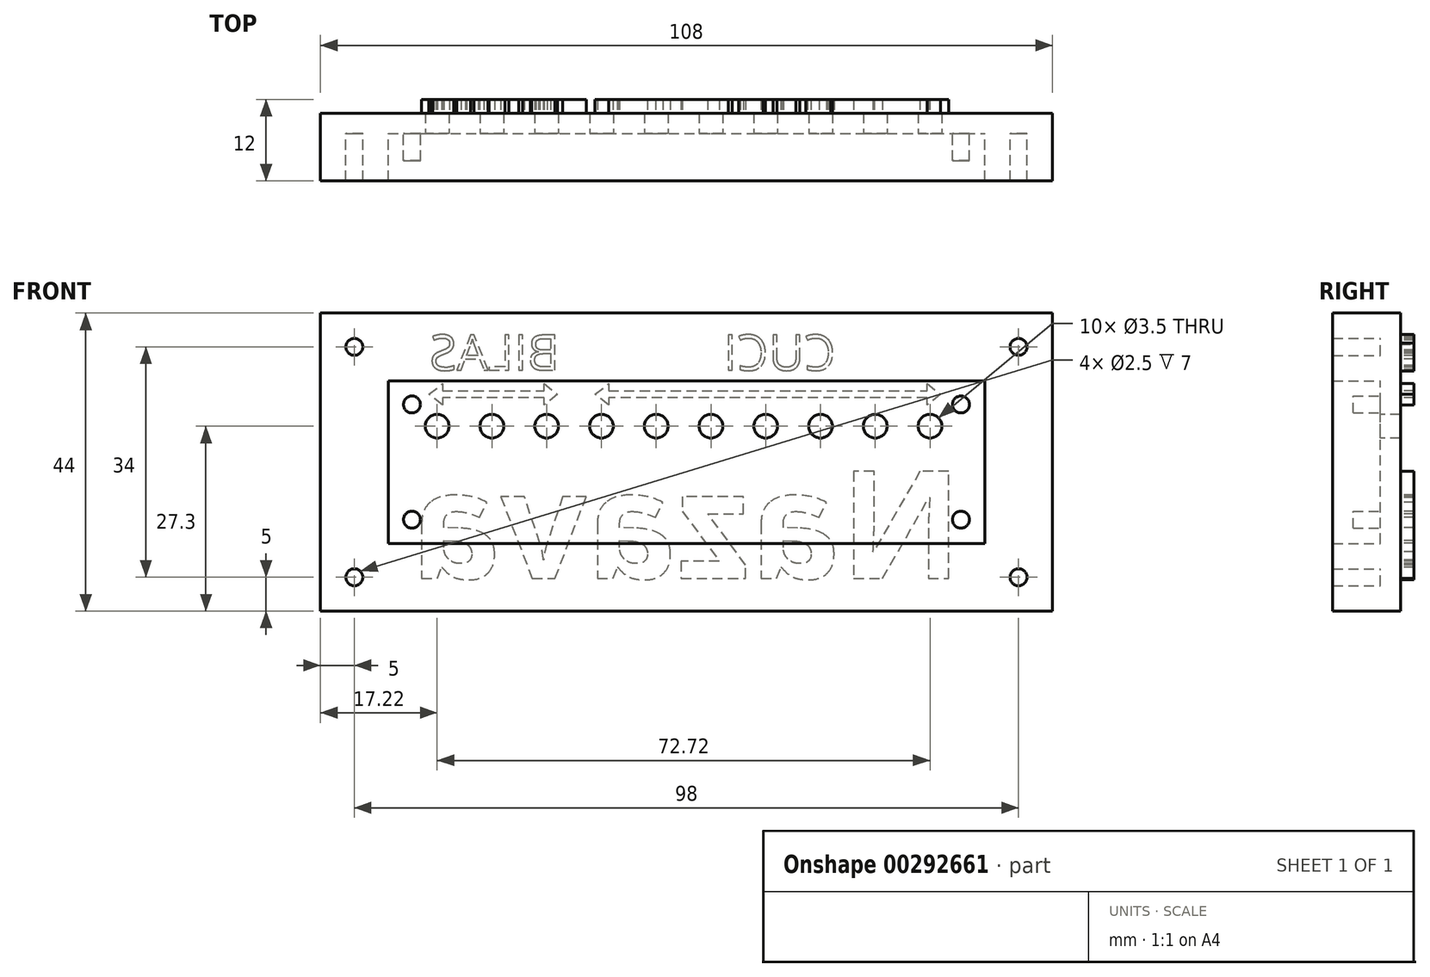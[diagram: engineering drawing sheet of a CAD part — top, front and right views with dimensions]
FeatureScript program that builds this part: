
annotation { "Feature Type Name" : "Feature", "Feature Type Description" : "" }
export const myFeature = defineFeature(function(context is Context, id is Id, definition is map)
    precondition{}
    {
        {
            var Q0;
            Q0=qCreatedBy(makeId("Front.planeOp"),FACE);
            var sketch = newSketch(context, id + "F0", { "sketchPlane" : qUnion([Q0])});
            skLineSegment(sketch, "E0.bottom", {"start": v(0, 0) * mm, "end": v(88, 0) * mm});
            skLineSegment(sketch, "E0.top", {"start": v(0, 24) * mm, "end": v(88, 24) * mm});
            skLineSegment(sketch, "E0.left", {"start": v(0, 0) * mm, "end": v(0, 24) * mm});
            skLineSegment(sketch, "E0.right", {"start": v(88, 0) * mm, "end": v(88, 24) * mm});
            skCircle(sketch, "E1", {"center": v(3.5, 20.5) * mm, "radius": 1.25 * mm});
            skCircle(sketch, "E2.0.1.0", {"center": v(3.5, 3.5) * mm, "radius": 1.25 * mm});
            skCircle(sketch, "E2.1.0.0", {"center": v(84.5, 20.5) * mm, "radius": 1.25 * mm});
            skCircle(sketch, "E2.1.1.0", {"center": v(84.5, 3.5) * mm, "radius": 1.25 * mm});
            skLineSegment(sketch, "E2.direction1", {"start": v(3.5, 20.5) * mm, "end": v(84.5, 20.5) * mm, "construction": true});
            skLineSegment(sketch, "E2.direction2", {"start": v(3.5, 20.5) * mm, "end": v(3.5, 3.5) * mm, "construction": true});
            skLineSegment(sketch, "E3.0", {"start": v(-10, 34) * mm, "end": v(98, 34) * mm});
            skLineSegment(sketch, "E3.1", {"start": v(-10, -10) * mm, "end": v(-10, 34) * mm});
            skLineSegment(sketch, "E3.2", {"start": v(-10, -10) * mm, "end": v(98, -10) * mm});
            skLineSegment(sketch, "E3.3", {"start": v(98, -10) * mm, "end": v(98, 34) * mm});
            skCircle(sketch, "E4", {"center": v(7.22, 17.3) * mm, "radius": 1.75 * mm});
            skCircle(sketch, "E5.1.0.0", {"center": v(15.3, 17.3) * mm, "radius": 1.75 * mm});
            skCircle(sketch, "E5.2.0.0", {"center": v(23.38, 17.3) * mm, "radius": 1.75 * mm});
            skCircle(sketch, "E5.3.0.0", {"center": v(31.46, 17.3) * mm, "radius": 1.75 * mm});
            skCircle(sketch, "E5.4.0.0", {"center": v(39.54, 17.3) * mm, "radius": 1.75 * mm});
            skCircle(sketch, "E5.5.0.0", {"center": v(47.62, 17.3) * mm, "radius": 1.75 * mm});
            skCircle(sketch, "E5.6.0.0", {"center": v(55.7, 17.3) * mm, "radius": 1.75 * mm});
            skCircle(sketch, "E5.7.0.0", {"center": v(63.78, 17.3) * mm, "radius": 1.75 * mm});
            skCircle(sketch, "E5.8.0.0", {"center": v(71.86, 17.3) * mm, "radius": 1.75 * mm});
            skCircle(sketch, "E5.9.0.0", {"center": v(79.94, 17.3) * mm, "radius": 1.75 * mm});
            skLineSegment(sketch, "E5.direction1", {"start": v(7.22, 17.3) * mm, "end": v(15.3, 17.3) * mm, "construction": true});
            skCircle(sketch, "E6", {"center": v(-5, 29) * mm, "radius": 1.25 * mm});
            skCircle(sketch, "E7.0.1.0", {"center": v(-5, -5) * mm, "radius": 1.25 * mm});
            skCircle(sketch, "E7.1.0.0", {"center": v(93, 29) * mm, "radius": 1.25 * mm});
            skCircle(sketch, "E7.1.1.0", {"center": v(93, -5) * mm, "radius": 1.25 * mm});
            skLineSegment(sketch, "E7.direction1", {"start": v(-5, 29) * mm, "end": v(93, 29) * mm, "construction": true});
            skLineSegment(sketch, "E7.direction2", {"start": v(-5, 29) * mm, "end": v(-5, -5) * mm, "construction": true});
            skSolve(sketch);
        }
        {
            var Q0;
            Q0=makeQuery(id+"F0.imprint","IMPRINT",FACE,{"disambiguationData":[TD([[makeQuery(id+"F0.imprint","IMPRINT",EDGE,{"derivedFrom":sQuery(id+"F0.wireOp",EDGE,"E0.bottom")}),-1.0]])]});
            var Q1;
            Q1=makeQuery(id+"F0.imprint","IMPRINT",FACE,{"disambiguationData":[TD([[makeQuery(id+"F0.imprint","IMPRINT",EDGE,{"derivedFrom":sQuery(id+"F0.wireOp",EDGE,"E0.bottom")}),1.0]])]});
            var Q2;
            Q2=makeQuery(id+"F0.imprint","IMPRINT",FACE,{"disambiguationData":[TD([[makeQuery(id+"F0.imprint","IMPRINT",EDGE,{"derivedFrom":sQuery(id+"F0.wireOp",EDGE,"E5.6.0.0")}),1.0]])]});
            var Q3;
            Q3=makeQuery(id+"F0.imprint","IMPRINT",FACE,{"disambiguationData":[TD([[makeQuery(id+"F0.imprint","IMPRINT",EDGE,{"derivedFrom":sQuery(id+"F0.wireOp",EDGE,"E2.1.1.0")}),1.0]])]});
            var Q4;
            Q4=makeQuery(id+"F0.imprint","IMPRINT",FACE,{"disambiguationData":[TD([[makeQuery(id+"F0.imprint","IMPRINT",EDGE,{"derivedFrom":sQuery(id+"F0.wireOp",EDGE,"E5.8.0.0")}),1.0]])]});
            var Q5;
            Q5=makeQuery(id+"F0.imprint","IMPRINT",FACE,{"disambiguationData":[TD([[makeQuery(id+"F0.imprint","IMPRINT",EDGE,{"derivedFrom":sQuery(id+"F0.wireOp",EDGE,"E5.7.0.0")}),1.0]])]});
            var Q6;
            Q6=makeQuery(id+"F0.imprint","IMPRINT",FACE,{"disambiguationData":[TD([[makeQuery(id+"F0.imprint","IMPRINT",EDGE,{"derivedFrom":sQuery(id+"F0.wireOp",EDGE,"E5.4.0.0")}),1.0]])]});
            var Q7;
            Q7=makeQuery(id+"F0.imprint","IMPRINT",FACE,{"disambiguationData":[TD([[makeQuery(id+"F0.imprint","IMPRINT",EDGE,{"derivedFrom":sQuery(id+"F0.wireOp",EDGE,"E5.5.0.0")}),1.0]])]});
            var Q8;
            Q8=makeQuery(id+"F0.imprint","IMPRINT",FACE,{"disambiguationData":[TD([[makeQuery(id+"F0.imprint","IMPRINT",EDGE,{"derivedFrom":sQuery(id+"F0.wireOp",EDGE,"E5.2.0.0")}),1.0]])]});
            var Q9;
            Q9=makeQuery(id+"F0.imprint","IMPRINT",FACE,{"disambiguationData":[TD([[makeQuery(id+"F0.imprint","IMPRINT",EDGE,{"derivedFrom":sQuery(id+"F0.wireOp",EDGE,"E5.9.0.0")}),1.0]])]});
            var Q10;
            Q10=makeQuery(id+"F0.imprint","IMPRINT",FACE,{"disambiguationData":[TD([[makeQuery(id+"F0.imprint","IMPRINT",EDGE,{"derivedFrom":sQuery(id+"F0.wireOp",EDGE,"E5.3.0.0")}),1.0]])]});
            var Q11;
            Q11=makeQuery(id+"F0.imprint","IMPRINT",FACE,{"disambiguationData":[TD([[makeQuery(id+"F0.imprint","IMPRINT",EDGE,{"derivedFrom":sQuery(id+"F0.wireOp",EDGE,"E2.0.1.0")}),1.0]])]});
            var Q12;
            Q12=makeQuery(id+"F0.imprint","IMPRINT",FACE,{"disambiguationData":[TD([[makeQuery(id+"F0.imprint","IMPRINT",EDGE,{"derivedFrom":sQuery(id+"F0.wireOp",EDGE,"E2.1.0.0")}),1.0]])]});
            var Q13;
            Q13=makeQuery(id+"F0.imprint","IMPRINT",FACE,{"disambiguationData":[TD([[makeQuery(id+"F0.imprint","IMPRINT",EDGE,{"derivedFrom":sQuery(id+"F0.wireOp",EDGE,"E5.1.0.0")}),1.0]])]});
            var Q14;
            Q14=makeQuery(id+"F0.imprint","IMPRINT",FACE,{"disambiguationData":[TD([[makeQuery(id+"F0.imprint","IMPRINT",EDGE,{"derivedFrom":sQuery(id+"F0.wireOp",EDGE,"E4")}),1.0]])]});
            var Q15;
            Q15=makeQuery(id+"F0.imprint","IMPRINT",FACE,{"disambiguationData":[TD([[makeQuery(id+"F0.imprint","IMPRINT",EDGE,{"derivedFrom":sQuery(id+"F0.wireOp",EDGE,"E1")}),1.0]])]});
            var Q16;
            Q16=makeQuery(id+"F0.imprint","IMPRINT",FACE,{"disambiguationData":[TD([[makeQuery(id+"F0.imprint","IMPRINT",EDGE,{"derivedFrom":sQuery(id+"F0.wireOp",EDGE,"E7.1.0.0")}),1.0]])]});
            var Q17;
            Q17=makeQuery(id+"F0.imprint","IMPRINT",FACE,{"disambiguationData":[TD([[makeQuery(id+"F0.imprint","IMPRINT",EDGE,{"derivedFrom":sQuery(id+"F0.wireOp",EDGE,"E6")}),1.0]])]});
            var Q18;
            Q18=makeQuery(id+"F0.imprint","IMPRINT",FACE,{"disambiguationData":[TD([[makeQuery(id+"F0.imprint","IMPRINT",EDGE,{"derivedFrom":sQuery(id+"F0.wireOp",EDGE,"E7.0.1.0")}),1.0]])]});
            var Q19;
            Q19=makeQuery(id+"F0.imprint","IMPRINT",FACE,{"disambiguationData":[TD([[makeQuery(id+"F0.imprint","IMPRINT",EDGE,{"derivedFrom":sQuery(id+"F0.wireOp",EDGE,"E7.1.1.0")}),1.0]])]});
            extrude(context, id + "F1", {"entities" : qUnion([Q0, Q1, Q2, Q3, Q4, Q5, Q6, Q7, Q8, Q9, Q10, Q11, Q12, Q13, Q14, Q15, Q16, Q17, Q18, Q19]), "oppositeDirection" : true, "depth" : 3 * mm, "offsetDistance" : 25 * mm});
        }
        {
            var Q0;
            Q0=makeQuery(id+"F0.imprint","IMPRINT",FACE,{"disambiguationData":[TD([[makeQuery(id+"F0.imprint","IMPRINT",EDGE,{"derivedFrom":sQuery(id+"F0.wireOp",EDGE,"E5.9.0.0")}),1.0]])]});
            var Q1;
            Q1=makeQuery(id+"F0.imprint","IMPRINT",FACE,{"disambiguationData":[TD([[makeQuery(id+"F0.imprint","IMPRINT",EDGE,{"derivedFrom":sQuery(id+"F0.wireOp",EDGE,"E5.8.0.0")}),1.0]])]});
            var Q2;
            Q2=makeQuery(id+"F0.imprint","IMPRINT",FACE,{"disambiguationData":[TD([[makeQuery(id+"F0.imprint","IMPRINT",EDGE,{"derivedFrom":sQuery(id+"F0.wireOp",EDGE,"E5.7.0.0")}),1.0]])]});
            var Q3;
            Q3=makeQuery(id+"F0.imprint","IMPRINT",FACE,{"disambiguationData":[TD([[makeQuery(id+"F0.imprint","IMPRINT",EDGE,{"derivedFrom":sQuery(id+"F0.wireOp",EDGE,"E5.6.0.0")}),1.0]])]});
            var Q4;
            Q4=makeQuery(id+"F0.imprint","IMPRINT",FACE,{"disambiguationData":[TD([[makeQuery(id+"F0.imprint","IMPRINT",EDGE,{"derivedFrom":sQuery(id+"F0.wireOp",EDGE,"E5.5.0.0")}),1.0]])]});
            var Q5;
            Q5=makeQuery(id+"F0.imprint","IMPRINT",FACE,{"disambiguationData":[TD([[makeQuery(id+"F0.imprint","IMPRINT",EDGE,{"derivedFrom":sQuery(id+"F0.wireOp",EDGE,"E5.4.0.0")}),1.0]])]});
            var Q6;
            Q6=makeQuery(id+"F0.imprint","IMPRINT",FACE,{"disambiguationData":[TD([[makeQuery(id+"F0.imprint","IMPRINT",EDGE,{"derivedFrom":sQuery(id+"F0.wireOp",EDGE,"E5.3.0.0")}),1.0]])]});
            var Q7;
            Q7=makeQuery(id+"F0.imprint","IMPRINT",FACE,{"disambiguationData":[TD([[makeQuery(id+"F0.imprint","IMPRINT",EDGE,{"derivedFrom":sQuery(id+"F0.wireOp",EDGE,"E5.2.0.0")}),1.0]])]});
            var Q8;
            Q8=makeQuery(id+"F0.imprint","IMPRINT",FACE,{"disambiguationData":[TD([[makeQuery(id+"F0.imprint","IMPRINT",EDGE,{"derivedFrom":sQuery(id+"F0.wireOp",EDGE,"E5.1.0.0")}),1.0]])]});
            var Q9;
            Q9=makeQuery(id+"F0.imprint","IMPRINT",FACE,{"disambiguationData":[TD([[makeQuery(id+"F0.imprint","IMPRINT",EDGE,{"derivedFrom":sQuery(id+"F0.wireOp",EDGE,"E4")}),1.0]])]});
            extrude(context, id + "F2", {"entities" : qUnion([Q0, Q1, Q2, Q3, Q4, Q5, Q6, Q7, Q8, Q9]), "operationType" : NewBodyOperationType.REMOVE, "endBound" : BoundingType.THROUGH_ALL, "oppositeDirection" : true, "depth" : 25 * mm, "offsetDistance" : 25 * mm});
        }
        {
            var Q0;
            Q0=makeQuery(id+"F0.imprint","IMPRINT",FACE,{"disambiguationData":[TD([[makeQuery(id+"F0.imprint","IMPRINT",EDGE,{"derivedFrom":sQuery(id+"F0.wireOp",EDGE,"E1")}),1.0]])]});
            var Q1;
            Q1=makeQuery(id+"F0.imprint","IMPRINT",FACE,{"disambiguationData":[TD([[makeQuery(id+"F0.imprint","IMPRINT",EDGE,{"derivedFrom":sQuery(id+"F0.wireOp",EDGE,"E2.1.0.0")}),1.0]])]});
            var Q2;
            Q2=makeQuery(id+"F0.imprint","IMPRINT",FACE,{"disambiguationData":[TD([[makeQuery(id+"F0.imprint","IMPRINT",EDGE,{"derivedFrom":sQuery(id+"F0.wireOp",EDGE,"E2.1.1.0")}),1.0]])]});
            var Q3;
            Q3=makeQuery(id+"F0.imprint","IMPRINT",FACE,{"disambiguationData":[TD([[makeQuery(id+"F0.imprint","IMPRINT",EDGE,{"derivedFrom":sQuery(id+"F0.wireOp",EDGE,"E2.0.1.0")}),1.0]])]});
            extrude(context, id + "F3", {"entities" : qUnion([Q0, Q1, Q2, Q3]), "operationType" : NewBodyOperationType.ADD, "depth" : 4 * mm, "offsetDistance" : 25 * mm});
        }
        {
            var Q0;
            Q0=makeQuery(id+"F0.imprint","IMPRINT",FACE,{"disambiguationData":[TD([[makeQuery(id+"F0.imprint","IMPRINT",EDGE,{"derivedFrom":sQuery(id+"F0.wireOp",EDGE,"E0.bottom")}),-1.0]])]});
            extrude(context, id + "F4", {"entities" : qUnion([Q0]), "operationType" : NewBodyOperationType.ADD, "depth" : 7 * mm, "offsetDistance" : 25 * mm});
        }
        {
            var Q0;
            Q0=makeQuery(id+"F1.opExtrude","CAP_FACE",FACE,{"disambiguationData":[OSD([sQuery(id+"F0.wireOp",EDGE,"E3.0"),sQuery(id+"F0.wireOp",EDGE,"E3.1"),sQuery(id+"F0.wireOp",EDGE,"E3.2"),sQuery(id+"F0.wireOp",EDGE,"E3.3")])],"isStart":false});
            var sketch = newSketch(context, id + "F5", { "sketchPlane" : qUnion([Q0])});
            skText(sketch, "E8", { "text": "Nazava", "fontName": "OpenSans-Bold.ttf"});
            const initialGuessF5  = {"E8": [-0.08468, -0.00517, 1, 0, 0.01592]};
            skSetInitialGuess(sketch, initialGuessF5);
            skSolve(sketch);
        }
        {
            var Q0;
            {var subQ0=sQuery(id+"F0.wireOp",EDGE,"E3.3");var subQ1=sQuery(id+"F0.wireOp",EDGE,"E3.0");var subQ2=sQuery(id+"F0.wireOp",EDGE,"E3.2");var subQ3=sQuery(id+"F0.wireOp",EDGE,"E3.1");Q0=makeQuery(id+"F8.boolean.opBoolean","SPLIT",FACE,{"disambiguationData":[TD([makeQuery(id+"F1.opExtrude","SWEPT_FACE",FACE,{"disambiguationData":[OSD([subQ1])]})])],"derivedFrom":makeQuery(id+"F1.opExtrude","CAP_FACE",FACE,{"disambiguationData":[OSD([subQ1,subQ3,subQ2,subQ0])],"isStart":false})});}
            var sketch = newSketch(context, id + "F6", { "sketchPlane" : qUnion([Q0])});
            skLineSegment(sketch, "E9", {"start": v(-30.5, 22) * mm, "end": v(-32.5, 23.57) * mm});
            skLineSegment(sketch, "E10", {"start": v(-32.5, 23.57) * mm, "end": v(-32.5, 22.5) * mm});
            skLineSegment(sketch, "E11", {"start": v(-32.5, 22.5) * mm, "end": v(-79.5, 22.5) * mm});
            skLineSegment(sketch, "E12", {"start": v(-79.5, 22.5) * mm, "end": v(-79.5, 23.57) * mm});
            skLineSegment(sketch, "E13", {"start": v(-79.5, 23.57) * mm, "end": v(-81.5, 22) * mm});
            skLineSegment(sketch, "E14", {"start": v(-81.5, 22) * mm, "end": v(-79.5, 20.43) * mm});
            skLineSegment(sketch, "E15", {"start": v(-79.5, 20.43) * mm, "end": v(-79.5, 21.5) * mm});
            skLineSegment(sketch, "E16", {"start": v(-79.5, 21.5) * mm, "end": v(-32.5, 21.5) * mm});
            skLineSegment(sketch, "E17", {"start": v(-32.5, 21.5) * mm, "end": v(-32.5, 20.43) * mm});
            skLineSegment(sketch, "E18", {"start": v(-32.5, 20.43) * mm, "end": v(-30.5, 22) * mm});
            skLineSegment(sketch, "E19", {"start": v(-5.99, 22) * mm, "end": v(-7.99, 23.57) * mm});
            skLineSegment(sketch, "E20", {"start": v(-7.99, 23.57) * mm, "end": v(-7.99, 22.5) * mm});
            skLineSegment(sketch, "E21", {"start": v(-7.99, 22.5) * mm, "end": v(-22.99, 22.5) * mm});
            skLineSegment(sketch, "E22", {"start": v(-22.99, 22.5) * mm, "end": v(-22.99, 23.57) * mm});
            skLineSegment(sketch, "E23", {"start": v(-22.99, 23.57) * mm, "end": v(-24.99, 22) * mm});
            skLineSegment(sketch, "E24", {"start": v(-24.99, 22) * mm, "end": v(-22.99, 20.43) * mm});
            skLineSegment(sketch, "E25", {"start": v(-22.99, 20.43) * mm, "end": v(-22.99, 21.5) * mm});
            skLineSegment(sketch, "E26", {"start": v(-22.99, 21.5) * mm, "end": v(-7.99, 21.5) * mm});
            skLineSegment(sketch, "E27", {"start": v(-7.99, 21.5) * mm, "end": v(-7.99, 20.43) * mm});
            skLineSegment(sketch, "E28", {"start": v(-7.99, 20.43) * mm, "end": v(-5.99, 22) * mm});
            skSolve(sketch);
        }
        {
            var Q0;
            {var subQ0=sQuery(id+"F0.wireOp",EDGE,"E3.0");var subQ1=sQuery(id+"F0.wireOp",EDGE,"E3.3");var subQ2=sQuery(id+"F0.wireOp",EDGE,"E3.2");var subQ3=sQuery(id+"F0.wireOp",EDGE,"E3.1");Q0=makeQuery(id+"F8.boolean.opBoolean","SPLIT",FACE,{"disambiguationData":[TD([makeQuery(id+"F1.opExtrude","SWEPT_FACE",FACE,{"disambiguationData":[OSD([subQ0])]})])],"derivedFrom":makeQuery(id+"F1.opExtrude","CAP_FACE",FACE,{"disambiguationData":[OSD([subQ0,subQ3,subQ2,subQ1])],"isStart":false})});}
            var sketch = newSketch(context, id + "F7", { "sketchPlane" : qUnion([Q0])});
            skText(sketch, "E29", { "text": "CUCI", "fontName": "OpenSans-Regular.ttf"});
            skText(sketch, "E30", { "text": "BILAS", "fontName": "OpenSans-Regular.ttf"});
            const initialGuessF7  = {"E29": [-0.06602, 0.02554, 1, 0, 0.00526], "E30": [-0.0253, 0.02554, 1, 0, 0.00526]};
            skSetInitialGuess(sketch, initialGuessF7);
            skSolve(sketch);
        }
        {
            var Q0;
            Q0 = qSketchRegion(id + "F5", true);
            var Q1;
            Q1 = qSketchRegion(id + "F6", true);
            var Q2;
            Q2 = qSketchRegion(id + "F7", true);
            extrude(context, id + "F8", {"entities" : qUnion([Q0, Q1, Q2]), "operationType" : NewBodyOperationType.ADD, "depth" : 2 * mm, "offsetDistance" : 25 * mm});
        }
    });
